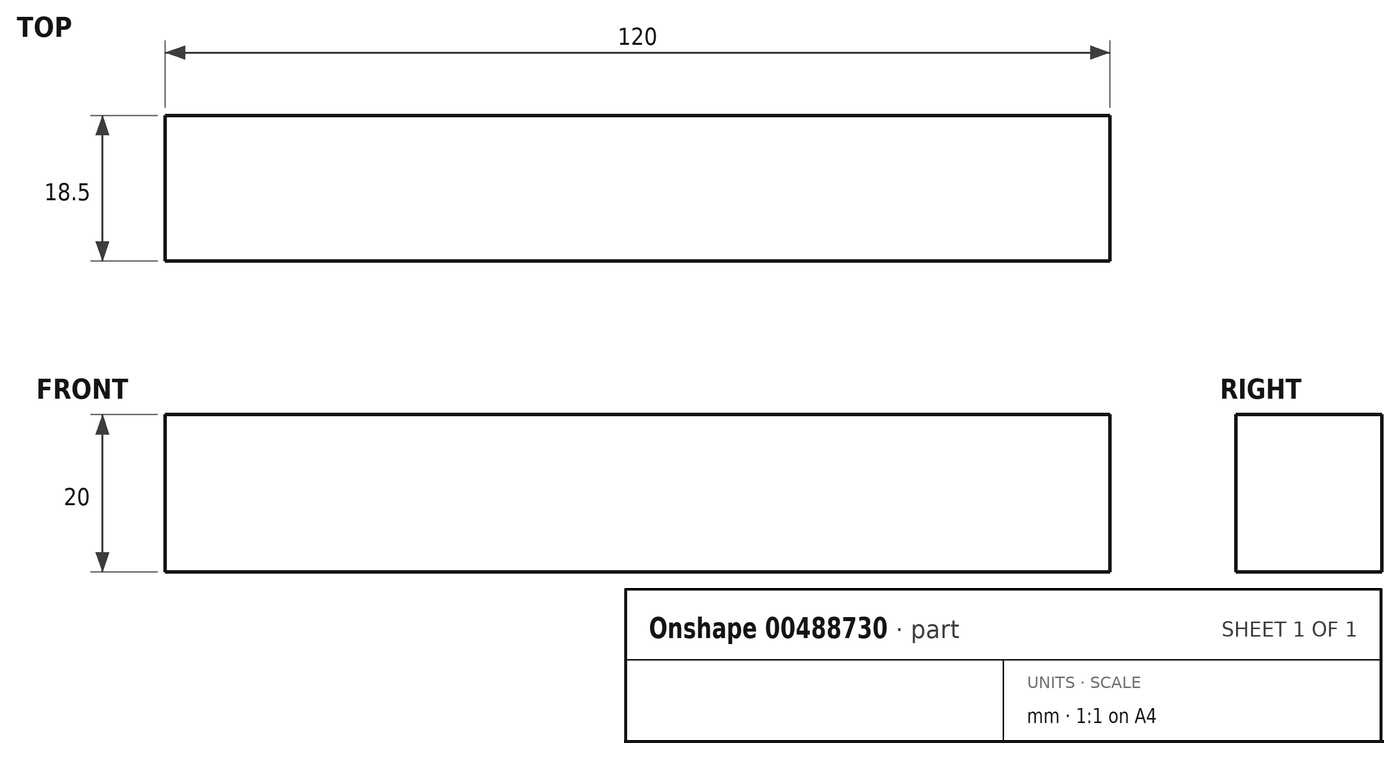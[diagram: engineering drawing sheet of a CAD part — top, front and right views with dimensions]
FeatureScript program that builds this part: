
annotation { "Feature Type Name" : "Feature", "Feature Type Description" : "" }
export const myFeature = defineFeature(function(context is Context, id is Id, definition is map)
    precondition{}
    {
        {
            var Q0;
            Q0=qCreatedBy(makeId("Top.planeOp"),FACE);
            var sketch = newSketch(context, id + "F0", { "sketchPlane" : qUnion([Q0])});
            skLineSegment(sketch, "E0.bottom", {"start": v(60, -9.25) * mm, "end": v(-60, -9.25) * mm});
            skLineSegment(sketch, "E0.top", {"start": v(60, 9.25) * mm, "end": v(-60, 9.25) * mm});
            skLineSegment(sketch, "E0.left", {"start": v(60, -9.25) * mm, "end": v(60, 9.25) * mm});
            skLineSegment(sketch, "E0.right", {"start": v(-60, -9.25) * mm, "end": v(-60, 9.25) * mm});
            skPoint(sketch, "E0.middle", {"position": v(0, 0) * mm});
            skSolve(sketch);
        }
        {
            var Q0;
            Q0=qSketchRegion(id+"F0",true);
            extrude(context, id + "F1", {"entities" : qUnion([Q0]), "endBound" : BoundingType.SYMMETRIC, "depth" : 20 * mm});
        }
    });
